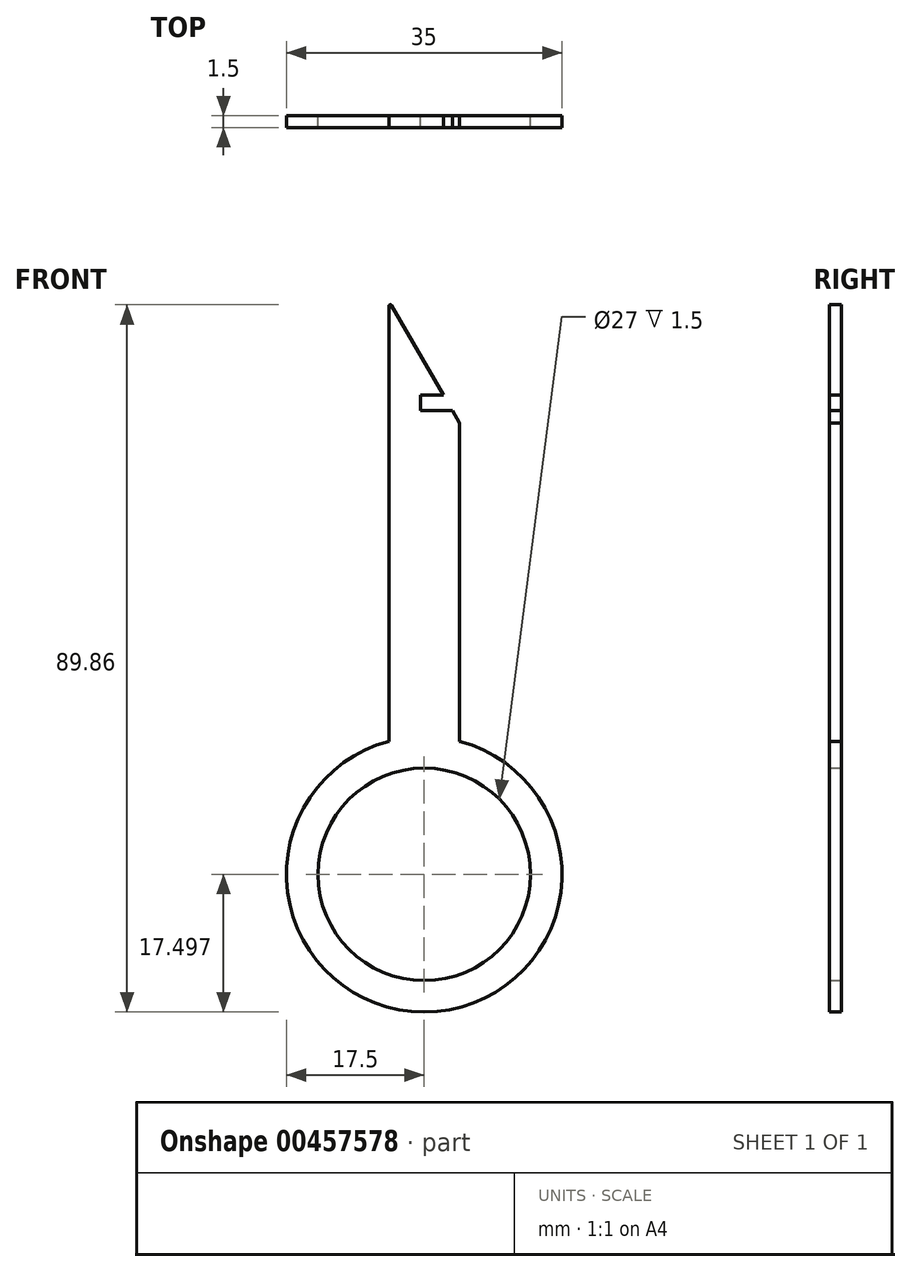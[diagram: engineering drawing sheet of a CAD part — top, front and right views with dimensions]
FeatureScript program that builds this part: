
annotation { "Feature Type Name" : "Feature", "Feature Type Description" : "" }
export const myFeature = defineFeature(function(context is Context, id is Id, definition is map)
    precondition{}
    {
        {
            var Q0;
            Q0=qCreatedBy(makeId("Front.planeOp"),FACE);
            var sketch = newSketch(context, id + "F0", { "sketchPlane" : qUnion([Q0])});
            skLineSegment(sketch, "E0", {"start": v(-8.63, 14.94) * mm, "end": v(-2.07, 3.59) * mm});
            skLineSegment(sketch, "E1", {"start": v(0, 0) * mm, "end": v(0, 0) * mm});
            skLineSegment(sketch, "E2", {"start": v(0, -40.41) * mm, "end": v(0, 0) * mm});
            skLineSegment(sketch, "E3", {"start": v(-9, 14.84) * mm, "end": v(-9, -40.41) * mm});
            skPoint(sketch, "E4.orphan", {"position": v(0, -81.81) * mm});
            skLineSegment(sketch, "E5", {"start": v(-2.07, 3.59) * mm, "end": v(-5, 3.59) * mm});
            skLineSegment(sketch, "E6", {"start": v(-5, 3.59) * mm, "end": v(-5, 1.59) * mm});
            skLineSegment(sketch, "E7", {"start": v(-5, 1.59) * mm, "end": v(-0.92, 1.59) * mm});
            skPoint(sketch, "E8.orphan", {"position": v(0, 1.59) * mm});
            skLineSegment(sketch, "E9.trimOffspring", {"start": v(-0.92, 1.59) * mm, "end": v(0, 0) * mm});
            skArc(sketch, "E10", {"start": v(-8.63, 14.94) * mm, "mid": v(-8.85, 15.04) * mm, "end": v(-9, 14.84) * mm});
            skPoint(sketch, "E11.orphan", {"position": v(-9, 15.59) * mm});
            skLineSegment(sketch, "E12", {"start": v(-9, 14.84) * mm, "end": v(-9, 15.59) * mm, "construction": true});
            skLineSegment(sketch, "E13", {"start": v(-8.63, 14.94) * mm, "end": v(-9, 15.59) * mm, "construction": true});
            skArc(sketch, "E14", {"start": v(-9, -40.41) * mm, "mid": v(-4.5, -74.82) * mm, "end": v(0, -40.41) * mm});
            skLineSegment(sketch, "E15", {"start": v(-9, -40.41) * mm, "end": v(-37.52, -40.41) * mm, "construction": true});
            skCircle(sketch, "E16", {"center": v(-4.5, -57.32) * mm, "radius": 13.5 * mm});
            skSolve(sketch);
        }
        {
            var Q0;
            Q0=makeQuery(id+"F0.imprint","IMPRINT",FACE,{"disambiguationData":[TD([[makeQuery(id+"F0.imprint","IMPRINT",EDGE,{"derivedFrom":sQuery(id+"F0.wireOp",EDGE,"E0")}),-1.0]])]});
            extrude(context, id + "F1", {"entities" : qUnion([Q0]), "depth" : 1.5 * mm});
        }
    });
